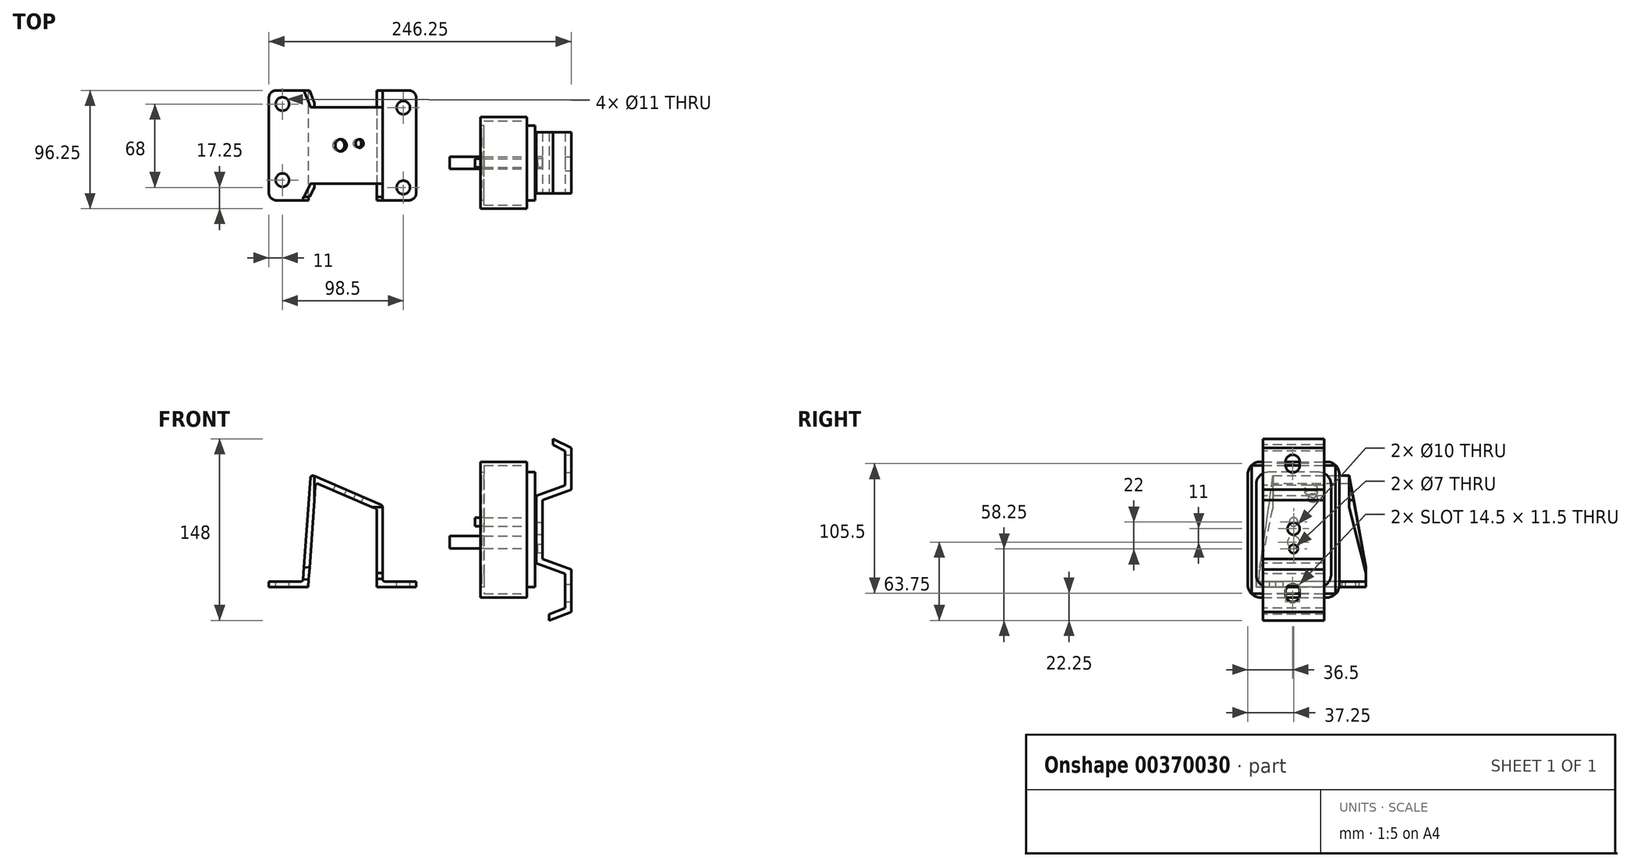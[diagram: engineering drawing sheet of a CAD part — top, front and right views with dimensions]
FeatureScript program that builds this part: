
annotation { "Feature Type Name" : "Feature", "Feature Type Description" : "" }
export const myFeature = defineFeature(function(context is Context, id is Id, definition is map)
    precondition{}
    {
        {
            var Q0;
            Q0=qCreatedBy(makeId("Front.planeOp"),FACE);
            var sketch = newSketch(context, id + "F0", { "sketchPlane" : qUnion([Q0])});
            skLineSegment(sketch, "E0", {"start": v(0, 0) * mm, "end": v(-120, 0) * mm});
            skPoint(sketch, "E1", {"position": v(-60, 0) * mm});
            skPoint(sketch, "E2", {"position": v(-32, 0) * mm});
            skPoint(sketch, "E3", {"position": v(-88, 0) * mm});
            skLineSegment(sketch, "E4", {"start": v(-32, 0) * mm, "end": v(-32, 63.5) * mm});
            skPoint(sketch, "E5", {"position": v(-82, 85) * mm});
            skLineSegment(sketch, "E6", {"start": v(-82, 85) * mm, "end": v(-88, 0) * mm});
            skLineSegment(sketch, "E7", {"start": v(-82, 85) * mm, "end": v(-32, 63.5) * mm});
            skLineSegment(sketch, "E8.0", {"start": v(-86.04, 91.64) * mm, "end": v(-92.49, 0.32) * mm});
            skLineSegment(sketch, "E8.1", {"start": v(-86.04, 91.64) * mm, "end": v(-27.5, 66.46) * mm});
            skLineSegment(sketch, "E8.2", {"start": v(-27.5, 0) * mm, "end": v(-27.5, 66.46) * mm});
            skLineSegment(sketch, "E9", {"start": v(-32, 0) * mm, "end": v(-27.5, 0) * mm});
            skPoint(sketch, "E10", {"position": v(-92.5, 0) * mm});
            skLineSegment(sketch, "E11", {"start": v(-92.5, 0) * mm, "end": v(-92.49, 0.32) * mm});
            skLineSegment(sketch, "E12", {"start": v(0, 0) * mm, "end": v(0, 4.5) * mm});
            skLineSegment(sketch, "E13", {"start": v(0, 4.5) * mm, "end": v(-27.5, 4.5) * mm});
            skLineSegment(sketch, "E14", {"start": v(-120, 0) * mm, "end": v(-120, 4.5) * mm});
            skLineSegment(sketch, "E15", {"start": v(-120, 4.5) * mm, "end": v(-92.2, 4.5) * mm});
            skSolve(sketch);
        }
        {
            var Q0;
            Q0=makeQuery(id+"F0.imprint","IMPRINT",FACE,{"disambiguationData":[TD([[makeQuery(id+"F0.imprint","IMPRINT",EDGE,{"derivedFrom":sQuery(id+"F0.wireOp",EDGE,"E4")}),-1.0]])]});
            var Q1;
            {var subQ0=sQuery(id+"F0.wireOp",EDGE,"E12");Q1=makeQuery(id+"F0.imprint","IMPRINT",FACE,{"disambiguationData":[TD([[makeQuery(id+"F0.imprint","IMPRINT",EDGE,{"derivedFrom":subQ0}),1.0]])]});}
            var Q2;
            {var subQ1=sQuery(id+"F0.wireOp",EDGE,"E11");Q2=makeQuery(id+"F0.imprint","IMPRINT",FACE,{"disambiguationData":[TD([[makeQuery(id+"F0.imprint","IMPRINT",EDGE,{"derivedFrom":subQ1}),1.0]])]});}
            extrude(context, id + "F1", {"entities" : qUnion([Q0, Q1, Q2]), "oppositeDirection" : true, "depth" : 89.5 * mm});
        }
        {
            var Q0;
            Q0=makeQuery(id+"F1.opExtrude","SWEPT_EDGE",EDGE,{"disambiguationData":[OSD([sQuery(id+"F0.wireOp",EDGE,"E8.0"),sQuery(id+"F0.wireOp",EDGE,"E8.1")])]});
            var Q1;
            Q1=makeQuery(id+"F1.opExtrude","SWEPT_EDGE",EDGE,{"disambiguationData":[OSD([sQuery(id+"F0.wireOp",EDGE,"E6"),sQuery(id+"F0.wireOp",EDGE,"E7")])]});
            var Q2;
            Q2=makeQuery(id+"F1.opExtrude","SWEPT_EDGE",EDGE,{"disambiguationData":[OSD([sQuery(id+"F0.wireOp",EDGE,"E4"),sQuery(id+"F0.wireOp",EDGE,"E7")])]});
            var Q3;
            Q3=makeQuery(id+"F1.opExtrude","SWEPT_EDGE",EDGE,{"disambiguationData":[OSD([sQuery(id+"F0.wireOp",EDGE,"E8.1"),sQuery(id+"F0.wireOp",EDGE,"E8.2")])]});
            var Q4;
            Q4=makeQuery(id+"F1.opExtrude","SWEPT_EDGE",EDGE,{"disambiguationData":[OSD([sQuery(id+"F0.wireOp",EDGE,"E8.0"),sQuery(id+"F0.wireOp",EDGE,"E15")])]});
            var Q5;
            Q5=makeQuery(id+"F1.opExtrude","SWEPT_EDGE",EDGE,{"disambiguationData":[OSD([sQuery(id+"F0.wireOp",EDGE,"E8.2"),sQuery(id+"F0.wireOp",EDGE,"E13")])]});
            fillet(context, id + "F2", {"entities" : qUnion([Q0, Q1, Q2, Q3, Q4, Q5]), "radius" : 2 * mm, "tangentPropagation" : true, "allowEdgeOverflow" : false});
        }
        {
            var Q0;
            Q0=makeQuery(id+"F1.opExtrude","SWEPT_FACE",FACE,{"disambiguationData":[OSD([sQuery(id+"F0.wireOp",EDGE,"E8.2")])]});
            var sketch = newSketch(context, id + "F3", { "sketchPlane" : qUnion([Q0])});
            skLineSegment(sketch, "E16.0", {"start": v(89.5, 90.52) * mm, "end": v(0, 90.52) * mm});
            skPoint(sketch, "E17", {"position": v(44.75, 90.52) * mm});
            skPoint(sketch, "E18", {"position": v(75.85, 90.52) * mm});
            skPoint(sketch, "E19", {"position": v(13.65, 90.52) * mm});
            skLineSegment(sketch, "E20.0", {"start": v(89.5, 65.15) * mm, "end": v(0, 65.15) * mm});
            skLineSegment(sketch, "E21.0", {"start": v(0, 6.5) * mm, "end": v(89.5, 6.5) * mm});
            skPoint(sketch, "E22", {"position": v(44.75, 6.5) * mm});
            skPoint(sketch, "E23", {"position": v(2.75, 6.5) * mm});
            skLineSegment(sketch, "E24", {"start": v(13.65, 90.52) * mm, "end": v(13.65, 65.15) * mm});
            skLineSegment(sketch, "E25", {"start": v(75.85, 90.52) * mm, "end": v(75.85, 65.15) * mm});
            skLineSegment(sketch, "E26.0", {"start": v(0, 6.5) * mm, "end": v(0, 65.15) * mm});
            skLineSegment(sketch, "E27.0", {"start": v(89.5, 6.5) * mm, "end": v(89.5, 65.15) * mm});
            skLineSegment(sketch, "E28.0", {"start": v(0, 90.52) * mm, "end": v(0, 66.98) * mm});
            skLineSegment(sketch, "E29.0", {"start": v(89.5, 90.52) * mm, "end": v(89.5, 66.98) * mm});
            skLineSegment(sketch, "E30", {"start": v(0, 66.98) * mm, "end": v(0, 65.15) * mm});
            skLineSegment(sketch, "E31", {"start": v(89.5, 66.98) * mm, "end": v(89.5, 65.15) * mm});
            skLineSegment(sketch, "E32", {"start": v(0, 90.52) * mm, "end": v(0, 93.52) * mm});
            skLineSegment(sketch, "E33", {"start": v(89.5, 6.5) * mm, "end": v(89.5, 11.5) * mm});
            skLineSegment(sketch, "E34", {"start": v(2.75, 6.5) * mm, "end": v(2.75, 11.5) * mm});
            skLineSegment(sketch, "E35", {"start": v(2.75, 11.5) * mm, "end": v(13.65, 65.15) * mm});
            skLineSegment(sketch, "E36", {"start": v(75.85, 65.15) * mm, "end": v(89.5, 11.5) * mm});
            skSolve(sketch);
        }
        {
            var Q0;
            {var subQ0=sQuery(id+"F3.wireOp",EDGE,"E25");Q0=makeQuery(id+"F3.imprint","IMPRINT",FACE,{"disambiguationData":[TD([[makeQuery(id+"F3.imprint","IMPRINT",EDGE,{"derivedFrom":subQ0}),1.0]])]});}
            var Q1;
            {var subQ0=sQuery(id+"F3.wireOp",EDGE,"E27.0");Q1=makeQuery(id+"F3.imprint","IMPRINT",FACE,{"disambiguationData":[TD([[makeQuery(id+"F3.imprint","IMPRINT",EDGE,{"derivedFrom":subQ0}),1.0]])]});}
            var Q2;
            {var subQ1=sQuery(id+"F3.wireOp",EDGE,"E26.0");Q2=makeQuery(id+"F3.imprint","IMPRINT",FACE,{"disambiguationData":[TD([[makeQuery(id+"F3.imprint","IMPRINT",EDGE,{"derivedFrom":subQ1}),-1.0]])]});}
            var Q3;
            {var subQ0=sQuery(id+"F3.wireOp",EDGE,"E24");Q3=makeQuery(id+"F3.imprint","IMPRINT",FACE,{"disambiguationData":[TD([[makeQuery(id+"F3.imprint","IMPRINT",EDGE,{"derivedFrom":subQ0}),-1.0]])]});}
            extrude(context, id + "F4", {"entities" : qUnion([Q0, Q1, Q2, Q3]), "operationType" : NewBodyOperationType.REMOVE, "oppositeDirection" : true, "depth" : 55.5 * mm});
        }
        {
            var Q0;
            Q0=makeQuery(id+"F4.boolean.opBoolean","COPY",EDGE,{"derivedFrom":makeQuery(id+"F4.opExtrude","SWEPT_EDGE",EDGE,{"disambiguationData":[OSD([sQuery(id+"F3.wireOp",EDGE,"E21.0"),sQuery(id+"F3.wireOp",EDGE,"E34")])]})});
            fillet(context, id + "F5", {"entities" : qUnion([Q0]), "radius" : 3 * mm, "tangentPropagation" : true, "allowEdgeOverflow" : false});
        }
        {
            var Q0;
            Q0=makeQuery(id+"F1.opExtrude","SWEPT_FACE",FACE,{"disambiguationData":[OSD([sQuery(id+"F0.wireOp",EDGE,"E8.0")])]});
            var sketch = newSketch(context, id + "F6", { "sketchPlane" : qUnion([Q0])});
            skLineSegment(sketch, "E37.0", {"start": v(-13.65, 84.26) * mm, "end": v(-13.65, 64.81) * mm});
            skLineSegment(sketch, "E38.0", {"start": v(-75.85, 84.26) * mm, "end": v(-75.85, 64.81) * mm});
            skLineSegment(sketch, "E39.1", {"start": v(-89.5, 4.55) * mm, "end": v(-89.5, 9.54) * mm});
            skLineSegment(sketch, "E40.0", {"start": v(-2.75, 7.53) * mm, "end": v(-2.75, 9.54) * mm});
            skLineSegment(sketch, "E41", {"start": v(-75.85, 84.26) * mm, "end": v(-89.5, 9.54) * mm});
            skLineSegment(sketch, "E42", {"start": v(-13.65, 84.26) * mm, "end": v(-2.75, 9.54) * mm});
            skLineSegment(sketch, "E43.0", {"start": v(-89.5, -0.14) * mm, "end": v(0, -0.14) * mm});
            skLineSegment(sketch, "E44", {"start": v(-2.75, 7.53) * mm, "end": v(-2.75, -0.14) * mm});
            skLineSegment(sketch, "E45.0", {"start": v(-89.5, 82.53) * mm, "end": v(-89.5, -0.14) * mm});
            skLineSegment(sketch, "E46.0", {"start": v(0, 82.53) * mm, "end": v(0, -0.14) * mm});
            skLineSegment(sketch, "E47.0", {"start": v(-89.5, 84.42) * mm, "end": v(0, 84.42) * mm});
            skLineSegment(sketch, "E48.0", {"start": v(-89.5, 82.53) * mm, "end": v(-89.5, 84.53) * mm});
            skLineSegment(sketch, "E49.0", {"start": v(0, 84.53) * mm, "end": v(0, 82.53) * mm});
            skLineSegment(sketch, "E50", {"start": v(-89.5, 84.42) * mm, "end": v(-89.5, 87.42) * mm});
            skLineSegment(sketch, "E51", {"start": v(-89.5, 87.42) * mm, "end": v(0, 87.42) * mm});
            skLineSegment(sketch, "E52", {"start": v(0, 87.42) * mm, "end": v(0, 84.42) * mm});
            skLineSegment(sketch, "E53", {"start": v(-13.65, 84.26) * mm, "end": v(-13.65, 87.42) * mm});
            skLineSegment(sketch, "E54", {"start": v(-75.85, 84.26) * mm, "end": v(-75.85, 87.42) * mm});
            skSolve(sketch);
        }
        {
            var Q0;
            {var subQ0=sQuery(id+"F6.wireOp",EDGE,"E45.0");var subQ1=sQuery(id+"F6.wireOp",EDGE,"E41");var subQ2=makeQuery(id+"F6.imprint","INTERSECT",VERTEX,{"derivedFrom":[subQ1,subQ0]});Q0=makeQuery(id+"F6.imprint","IMPRINT",FACE,{"disambiguationData":[TD([[makeQuery(id+"F6.imprint","IMPRINT",EDGE,{"disambiguationData":[TD([[subQ2,1.0]])],"derivedFrom":subQ1}),-1.0]])]});}
            var Q1;
            {var subQ0=sQuery(id+"F6.wireOp",EDGE,"E50");var subQ5=sQuery(id+"F6.wireOp",EDGE,"E51");var subQ6=makeQuery(id+"F6.imprint","INTERSECT",VERTEX,{"derivedFrom":[subQ0,subQ5]});Q1=makeQuery(id+"F6.imprint","IMPRINT",FACE,{"disambiguationData":[TD([[makeQuery(id+"F6.imprint","IMPRINT",EDGE,{"disambiguationData":[TD([[subQ6,-1.0]])],"derivedFrom":subQ5}),-1.0]])]});}
            var Q2;
            {var subQ8=sQuery(id+"F6.wireOp",EDGE,"E48.0");Q2=makeQuery(id+"F6.imprint","IMPRINT",FACE,{"disambiguationData":[TD([[makeQuery(id+"F6.imprint","IMPRINT",EDGE,{"derivedFrom":subQ8}),-1.0]])]});}
            var Q3;
            {var subQ0=sQuery(id+"F6.wireOp",EDGE,"E52");var subQ5=sQuery(id+"F6.wireOp",EDGE,"E51");var subQ6=makeQuery(id+"F6.imprint","INTERSECT",VERTEX,{"derivedFrom":[subQ5,subQ0]});Q3=makeQuery(id+"F6.imprint","IMPRINT",FACE,{"disambiguationData":[TD([[makeQuery(id+"F6.imprint","IMPRINT",EDGE,{"disambiguationData":[TD([[subQ6,1.0]])],"derivedFrom":subQ5}),-1.0]])]});}
            var Q4;
            {var subQ5=sQuery(id+"F6.wireOp",EDGE,"E49.0");Q4=makeQuery(id+"F6.imprint","IMPRINT",FACE,{"disambiguationData":[TD([[makeQuery(id+"F6.imprint","IMPRINT",EDGE,{"derivedFrom":subQ5}),-1.0]])]});}
            var Q5;
            {var subQ4=sQuery(id+"F6.wireOp",EDGE,"E40.0");Q5=makeQuery(id+"F6.imprint","IMPRINT",FACE,{"disambiguationData":[TD([[makeQuery(id+"F6.imprint","IMPRINT",EDGE,{"derivedFrom":subQ4}),-1.0]])]});}
            extrude(context, id + "F7", {"entities" : qUnion([Q0, Q1, Q2, Q3, Q4, Q5]), "operationType" : NewBodyOperationType.REMOVE, "oppositeDirection" : true, "depth" : 25 * mm});
        }
        {
            var Q0;
            Q0=makeQuery(id+"F1.opExtrude","SWEPT_FACE",FACE,{"disambiguationData":[OSD([sQuery(id+"F0.wireOp",EDGE,"E13")])]});
            var sketch = newSketch(context, id + "F8", { "sketchPlane" : qUnion([Q0])});
            skPoint(sketch, "E55", {"position": v(-10.5, 75.5) * mm});
            skPoint(sketch, "E56", {"position": v(-10.5, 10.5) * mm});
            skCircle(sketch, "E57", {"center": v(-10.5, 10.5) * mm, "radius": 5.5 * mm});
            skCircle(sketch, "E58", {"center": v(-10.5, 75.5) * mm, "radius": 5.5 * mm});
            skSolve(sketch);
        }
        {
            var Q0;
            Q0=qSketchRegion(id+"F8",true);
            extrude(context, id + "F9", {"entities" : qUnion([Q0]), "operationType" : NewBodyOperationType.REMOVE, "oppositeDirection" : true, "depth" : 5 * mm});
        }
        {
            var Q0;
            Q0=makeQuery(id+"F1.opExtrude","SWEPT_FACE",FACE,{"disambiguationData":[OSD([sQuery(id+"F0.wireOp",EDGE,"E15")])]});
            var sketch = newSketch(context, id + "F10", { "sketchPlane" : qUnion([Q0])});
            skPoint(sketch, "E59", {"position": v(-109, 78.5) * mm});
            skPoint(sketch, "E60", {"position": v(-109, 16.5) * mm});
            skCircle(sketch, "E61", {"center": v(-109, 16.5) * mm, "radius": 5.5 * mm});
            skCircle(sketch, "E62", {"center": v(-109, 78.5) * mm, "radius": 5.5 * mm});
            skSolve(sketch);
        }
        {
            var Q0;
            Q0=qSketchRegion(id+"F10",true);
            extrude(context, id + "F11", {"entities" : qUnion([Q0]), "operationType" : NewBodyOperationType.REMOVE, "oppositeDirection" : true, "depth" : 5 * mm});
        }
        {
            var Q0;
            Q0=makeQuery(id+"F1.opExtrude","SWEPT_FACE",FACE,{"disambiguationData":[OSD([sQuery(id+"F0.wireOp",EDGE,"E8.1")])]});
            var sketch = newSketch(context, id + "F12", { "sketchPlane" : qUnion([Q0])});
            skPoint(sketch, "E63", {"position": v(-88.32, 44.85) * mm});
            skCircle(sketch, "E64", {"center": v(-88.32, 44.85) * mm, "radius": 5 * mm});
            skPoint(sketch, "E65", {"position": v(-71.82, 46.35) * mm});
            skCircle(sketch, "E66", {"center": v(-71.82, 46.35) * mm, "radius": 3.5 * mm});
            skSolve(sketch);
        }
        {
            var Q0;
            Q0=qSketchRegion(id+"F12",true);
            extrude(context, id + "F13", {"entities" : qUnion([Q0]), "operationType" : NewBodyOperationType.REMOVE, "oppositeDirection" : true, "depth" : 5 * mm});
        }
        {
            var Q0;
            Q0=makeQuery(id+"F1.opExtrude","CAP_EDGE",EDGE,{"disambiguationData":[OSD([sQuery(id+"F0.wireOp",EDGE,"E12")])],"isStart":false});
            var Q1;
            Q1=makeQuery(id+"F1.opExtrude","CAP_EDGE",EDGE,{"disambiguationData":[OSD([sQuery(id+"F0.wireOp",EDGE,"E12")])],"isStart":true});
            var Q2;
            Q2=makeQuery(id+"F1.opExtrude","CAP_EDGE",EDGE,{"disambiguationData":[OSD([sQuery(id+"F0.wireOp",EDGE,"E14")])],"isStart":true});
            var Q3;
            Q3=makeQuery(id+"F1.opExtrude","CAP_EDGE",EDGE,{"disambiguationData":[OSD([sQuery(id+"F0.wireOp",EDGE,"E14")])],"isStart":false});
            fillet(context, id + "F14", {"entities" : qUnion([Q0, Q1, Q2, Q3]), "radius" : 6 * mm, "tangentPropagation" : true, "allowEdgeOverflow" : false});
        }
        {
            var Q0;
            Q0=qCreatedBy(makeId("Front.planeOp"),FACE);
            var sketch = newSketch(context, id + "F15", { "sketchPlane" : qUnion([Q0])});
            skPoint(sketch, "E67", {"position": v(75, 0) * mm});
            skLineSegment(sketch, "E68", {"start": v(75, 0) * mm, "end": v(96.75, 0) * mm});
            skLineSegment(sketch, "E69", {"start": v(75, 0) * mm, "end": v(53.25, 0) * mm});
            skLineSegment(sketch, "E70", {"start": v(53.25, 0) * mm, "end": v(53.25, 93.5) * mm});
            skLineSegment(sketch, "E71", {"start": v(53.25, 93.5) * mm, "end": v(96.75, 93.5) * mm});
            skLineSegment(sketch, "E72", {"start": v(96.75, 93.5) * mm, "end": v(96.75, 0) * mm});
            skSolve(sketch);
        }
        {
            var Q0;
            Q0=qSketchRegion(id+"F15",true);
            extrude(context, id + "F16", {"entities" : qUnion([Q0]), "oppositeDirection" : true, "depth" : 61 * mm});
        }
        {
            var Q0;
            Q0=makeQuery(id+"F16.opExtrude","SWEPT_FACE",FACE,{"disambiguationData":[OSD([sQuery(id+"F15.wireOp",EDGE,"E72")])]});
            var sketch = newSketch(context, id + "F17", { "sketchPlane" : qUnion([Q0])});
            skPoint(sketch, "E73", {"position": v(30.5, 47.5) * mm});
            skCircle(sketch, "E74", {"center": v(30.5, 47.5) * mm, "radius": 5 * mm});
            skPoint(sketch, "E75", {"position": v(30.5, 31) * mm});
            skCircle(sketch, "E76", {"center": v(30.5, 31) * mm, "radius": 3.5 * mm});
            skSolve(sketch);
        }
        {
            var Q0;
            Q0=makeQuery(id+"F17.imprint","IMPRINT",FACE,{"disambiguationData":[TD([[makeQuery(id+"F17.imprint","IMPRINT",EDGE,{"derivedFrom":sQuery(id+"F17.wireOp",EDGE,"E74")}),1.0]])]});
            extrude(context, id + "F18", {"entities" : qUnion([Q0]), "operationType" : NewBodyOperationType.ADD, "depth" : 20 * mm});
        }
        {
            var Q0;
            Q0=qSketchRegion(id+"F17",true);
            extrude(context, id + "F19", {"entities" : qUnion([Q0]), "operationType" : NewBodyOperationType.ADD, "depth" : 2.25 * mm});
        }
        {
            var Q0;
            Q0=makeQuery(id+"F16.opExtrude","SWEPT_FACE",FACE,{"disambiguationData":[OSD([sQuery(id+"F15.wireOp",EDGE,"E70")])]});
            var sketch = newSketch(context, id + "F20", { "sketchPlane" : qUnion([Q0])});
            skPoint(sketch, "E77", {"position": v(-30.5, 36.5) * mm});
            skPoint(sketch, "E78", {"position": v(-30.5, 53) * mm});
            skCircle(sketch, "E79", {"center": v(-30.5, 36.5) * mm, "radius": 5 * mm});
            skCircle(sketch, "E80", {"center": v(-30.5, 53) * mm, "radius": 3.5 * mm});
            skSolve(sketch);
        }
        {
            var Q0;
            Q0=makeQuery(id+"F20.imprint","IMPRINT",FACE,{"disambiguationData":[TD([[makeQuery(id+"F20.imprint","IMPRINT",EDGE,{"derivedFrom":sQuery(id+"F20.wireOp",EDGE,"E79")}),1.0]])]});
            extrude(context, id + "F21", {"entities" : qUnion([Q0]), "operationType" : NewBodyOperationType.ADD, "depth" : 26 * mm});
        }
        {
            var Q0;
            Q0=qSketchRegion(id+"F20",true);
            extrude(context, id + "F22", {"entities" : qUnion([Q0]), "operationType" : NewBodyOperationType.ADD, "depth" : 5.5 * mm});
        }
        {
            var Q0;
            Q0=makeQuery(id+"F16.opExtrude","CAP_EDGE",EDGE,{"disambiguationData":[OSD([sQuery(id+"F15.wireOp",EDGE,"E71")])],"isStart":true});
            var Q1;
            Q1=makeQuery(id+"F16.opExtrude","CAP_EDGE",EDGE,{"disambiguationData":[OSD([sQuery(id+"F15.wireOp",EDGE,"E71")])],"isStart":false});
            var Q2;
            Q2=makeQuery(id+"F16.opExtrude","CAP_EDGE",EDGE,{"disambiguationData":[OSD([sQuery(id+"F15.wireOp",EDGE,"E68"),sQuery(id+"F15.wireOp",EDGE,"E69")])],"isStart":false});
            var Q3;
            Q3=makeQuery(id+"F16.opExtrude","CAP_EDGE",EDGE,{"disambiguationData":[OSD([sQuery(id+"F15.wireOp",EDGE,"E68"),sQuery(id+"F15.wireOp",EDGE,"E69")])],"isStart":true});
            fillet(context, id + "F23", {"entities" : qUnion([Q0, Q1, Q2, Q3]), "radius" : 10 * mm, "tangentPropagation" : true, "allowEdgeOverflow" : false});
        }
        {
            var Q0;
            Q0=makeQuery(id+"F16.opExtrude","SWEPT_FACE",FACE,{"disambiguationData":[OSD([sQuery(id+"F15.wireOp",EDGE,"E70")])]});
            cPlane(context, id + "F24", {"entities" : qUnion([Q0]), "cplaneType" : CPlaneType.OFFSET, "offset" : 1 * mm, "width" : 150 * mm, "height" : 150 * mm});
        }
        {
            var Q0;
            Q0=qCreatedBy(id+"F24.planeOp",FACE);
            var sketch = newSketch(context, id + "F25", { "sketchPlane" : qUnion([Q0])});
            skLineSegment(sketch, "E81.0", {"start": v(-51, 93.5) * mm, "end": v(-10, 93.5) * mm});
            skLineSegment(sketch, "E82.0", {"start": v(-61, 10) * mm, "end": v(-61, 83.5) * mm});
            skPoint(sketch, "E83", {"position": v(-30.5, 46.75) * mm});
            skPoint(sketch, "E83.positionSnap0", {"position": v(-61, 46.75) * mm});
            skPoint(sketch, "E83.positionSnap1", {"position": v(-30.5, 93.5) * mm});
            skLineSegment(sketch, "E84.bottom", {"start": v(6.75, 102) * mm, "end": v(-67.75, 102) * mm});
            skLineSegment(sketch, "E84.top", {"start": v(6.75, -8.5) * mm, "end": v(-67.75, -8.5) * mm});
            skLineSegment(sketch, "E84.left", {"start": v(6.75, 102) * mm, "end": v(6.75, -8.5) * mm});
            skLineSegment(sketch, "E84.right", {"start": v(-67.75, 102) * mm, "end": v(-67.75, -8.5) * mm});
            skCircle(sketch, "E85.0", {"center": v(-30.5, 36.5) * mm, "radius": 5 * mm});
            skCircle(sketch, "E86.0", {"center": v(-30.5, 53) * mm, "radius": 3.5 * mm});
            skSolve(sketch);
        }
        {
            var Q0;
            Q0=qSketchRegion(id+"F25",true);
            extrude(context, id + "F26", {"entities" : qUnion([Q0]), "oppositeDirection" : true, "depth" : 38 * mm});
        }
        {
            var Q0;
            Q0=makeQuery(id+"F26.opExtrude","CAP_FACE",FACE,{"disambiguationData":[OSD([sQuery(id+"F25.wireOp",EDGE,"E84.bottom"),sQuery(id+"F25.wireOp",EDGE,"E84.top"),sQuery(id+"F25.wireOp",EDGE,"E84.left"),sQuery(id+"F25.wireOp",EDGE,"E84.right")])],"isStart":false});
            var sketch = newSketch(context, id + "F27", { "sketchPlane" : qUnion([Q0])});
            skLineSegment(sketch, "E87.0", {"start": v(-6.75, 102) * mm, "end": v(67.75, 102) * mm});
            skLineSegment(sketch, "E88.0", {"start": v(-6.75, 102) * mm, "end": v(-6.75, -8.5) * mm});
            skLineSegment(sketch, "E89.0", {"start": v(67.75, 102) * mm, "end": v(67.75, -8.5) * mm});
            skLineSegment(sketch, "E90.0", {"start": v(-6.75, -8.5) * mm, "end": v(67.75, -8.5) * mm});
            skLineSegment(sketch, "E91.0", {"start": v(-3.75, 99) * mm, "end": v(64.75, 99) * mm});
            skLineSegment(sketch, "E91.1", {"start": v(-3.75, 99) * mm, "end": v(-3.75, -5.5) * mm});
            skLineSegment(sketch, "E91.2", {"start": v(-3.75, -5.5) * mm, "end": v(64.75, -5.5) * mm});
            skLineSegment(sketch, "E91.3", {"start": v(64.75, 99) * mm, "end": v(64.75, -5.5) * mm});
            skSolve(sketch);
        }
        {
            var Q0;
            Q0=makeQuery(id+"F27.imprint","IMPRINT",FACE,{"disambiguationData":[TD([[makeQuery(id+"F27.imprint","IMPRINT",EDGE,{"derivedFrom":sQuery(id+"F27.wireOp",EDGE,"E91.0")}),-1.0]])]});
            extrude(context, id + "F28", {"entities" : qUnion([Q0]), "operationType" : NewBodyOperationType.REMOVE, "oppositeDirection" : true, "depth" : 35 * mm});
        }
        {
            var Q0;
            Q0=makeQuery(id+"F26.opExtrude","SWEPT_EDGE",EDGE,{"disambiguationData":[OSD([sQuery(id+"F25.wireOp",EDGE,"E84.bottom"),sQuery(id+"F25.wireOp",EDGE,"E84.left")])]});
            var Q1;
            Q1=makeQuery(id+"F26.opExtrude","SWEPT_EDGE",EDGE,{"disambiguationData":[OSD([sQuery(id+"F25.wireOp",EDGE,"E84.bottom"),sQuery(id+"F25.wireOp",EDGE,"E84.right")])]});
            var Q2;
            Q2=makeQuery(id+"F26.opExtrude","SWEPT_EDGE",EDGE,{"disambiguationData":[OSD([sQuery(id+"F25.wireOp",EDGE,"E84.top"),sQuery(id+"F25.wireOp",EDGE,"E84.right")])]});
            var Q3;
            Q3=makeQuery(id+"F26.opExtrude","SWEPT_EDGE",EDGE,{"disambiguationData":[OSD([sQuery(id+"F25.wireOp",EDGE,"E84.top"),sQuery(id+"F25.wireOp",EDGE,"E84.left")])]});
            fillet(context, id + "F29", {"entities" : qUnion([Q0, Q1, Q2, Q3]), "radius" : 10 * mm, "tangentPropagation" : true, "allowEdgeOverflow" : false});
        }
        {
            var Q0;
            Q0=makeQuery(id+"F16.opExtrude","SWEPT_FACE",FACE,{"disambiguationData":[OSD([sQuery(id+"F15.wireOp",EDGE,"E72")])]});
            cPlane(context, id + "F30", {"entities" : qUnion([Q0]), "cplaneType" : CPlaneType.OFFSET, "offset" : 1 * mm, "width" : 150 * mm, "height" : 150 * mm});
        }
        {
            var Q0;
            Q0=qCreatedBy(id+"F30.planeOp",FACE);
            var sketch = newSketch(context, id + "F31", { "sketchPlane" : qUnion([Q0])});
            skLineSegment(sketch, "E92.0", {"start": v(61, 83.5) * mm, "end": v(61, 10) * mm});
            skLineSegment(sketch, "E93.0", {"start": v(51, 0) * mm, "end": v(10, 0) * mm});
            skPoint(sketch, "E94", {"position": v(30.5, 46.75) * mm});
            skPoint(sketch, "E94.positionSnap0", {"position": v(30.5, 0) * mm});
            skPoint(sketch, "E94.positionSnap1", {"position": v(61, 46.75) * mm});
            skLineSegment(sketch, "E95.bottom", {"start": v(55.5, -27.25) * mm, "end": v(5.5, -27.25) * mm});
            skLineSegment(sketch, "E95.top", {"start": v(55.5, 120.75) * mm, "end": v(5.5, 120.75) * mm});
            skLineSegment(sketch, "E95.left", {"start": v(55.5, -27.25) * mm, "end": v(55.5, 120.75) * mm});
            skLineSegment(sketch, "E95.right", {"start": v(5.5, -27.25) * mm, "end": v(5.5, 120.75) * mm});
            skCircle(sketch, "E96.0.0", {"center": v(30.5, 31) * mm, "radius": 3.5 * mm});
            skCircle(sketch, "E97.0", {"center": v(30.5, 47.5) * mm, "radius": 5 * mm});
            skSolve(sketch);
        }
        {
            var Q0;
            Q0=qSketchRegion(id+"F31",true);
            extrude(context, id + "F32", {"entities" : qUnion([Q0]), "depth" : 28.5 * mm});
        }
        {
            var Q0;
            Q0=makeQuery(id+"F32.opExtrude","SWEPT_FACE",FACE,{"disambiguationData":[OSD([sQuery(id+"F31.wireOp",EDGE,"E95.right")])]});
            var sketch = newSketch(context, id + "F33", { "sketchPlane" : qUnion([Q0])});
            skLineSegment(sketch, "E98.0", {"start": v(126.25, -27.25) * mm, "end": v(126.25, 120.75) * mm});
            skPoint(sketch, "E99", {"position": v(97.75, 46.75) * mm});
            skPoint(sketch, "E100", {"position": v(97.75, 74.25) * mm});
            skPoint(sketch, "E101", {"position": v(97.75, 19.25) * mm});
            skPoint(sketch, "E102", {"position": v(121.25, -27.25) * mm});
            skLineSegment(sketch, "E103", {"start": v(121.25, -27.25) * mm, "end": v(121.25, 120.75) * mm, "construction": true});
            skPoint(sketch, "E104", {"position": v(121.25, 46.75) * mm});
            skPoint(sketch, "E105", {"position": v(121.25, 82.75) * mm});
            skPoint(sketch, "E106", {"position": v(121.25, 10.75) * mm});
            skPoint(sketch, "E107", {"position": v(121.25, -17.25) * mm});
            skPoint(sketch, "E108", {"position": v(121.25, 110.75) * mm});
            skLineSegment(sketch, "E109", {"start": v(97.75, 19.25) * mm, "end": v(121.25, 10.75) * mm});
            skLineSegment(sketch, "E110", {"start": v(121.25, 10.75) * mm, "end": v(121.25, -17.25) * mm});
            skLineSegment(sketch, "E111", {"start": v(97.75, 19.25) * mm, "end": v(97.75, 74.25) * mm});
            skLineSegment(sketch, "E112", {"start": v(97.75, 74.25) * mm, "end": v(121.25, 82.75) * mm});
            skLineSegment(sketch, "E113", {"start": v(121.25, 82.75) * mm, "end": v(121.25, 110.75) * mm});
            skPoint(sketch, "E114", {"position": v(111.25, 120.75) * mm});
            skPoint(sketch, "E115", {"position": v(108.25, -27.25) * mm});
            skLineSegment(sketch, "E116", {"start": v(108.25, -27.25) * mm, "end": v(108.25, -22.25) * mm});
            skLineSegment(sketch, "E117", {"start": v(108.25, -22.25) * mm, "end": v(121.25, -17.25) * mm});
            skLineSegment(sketch, "E118", {"start": v(111.25, 120.75) * mm, "end": v(111.25, 115.75) * mm});
            skLineSegment(sketch, "E119", {"start": v(111.25, 115.75) * mm, "end": v(121.25, 110.75) * mm});
            skLineSegment(sketch, "E120.1", {"start": v(102.75, 22.76) * mm, "end": v(102.75, 70.74) * mm});
            skLineSegment(sketch, "E121", {"start": v(108.25, -27.25) * mm, "end": v(126.25, -20.33) * mm});
            skLineSegment(sketch, "E122", {"start": v(111.25, 120.75) * mm, "end": v(126.25, 113.25) * mm});
            skLineSegment(sketch, "E123", {"start": v(126.25, 113.25) * mm, "end": v(126.25, -20.33) * mm});
            skLineSegment(sketch, "E124", {"start": v(102.75, 22.76) * mm, "end": v(126.25, 14.26) * mm});
            skLineSegment(sketch, "E125", {"start": v(102.75, 70.74) * mm, "end": v(126.25, 79.24) * mm});
            skLineSegment(sketch, "E126.0", {"start": v(126.25, 120.75) * mm, "end": v(97.75, 120.75) * mm});
            skLineSegment(sketch, "E127.0", {"start": v(97.75, -27.25) * mm, "end": v(97.75, 120.75) * mm});
            skLineSegment(sketch, "E128.0", {"start": v(126.25, -27.25) * mm, "end": v(97.75, -27.25) * mm});
            skSolve(sketch);
        }
        {
            var Q0;
            {var subQ3=sQuery(id+"F33.wireOp",EDGE,"E122");Q0=makeQuery(id+"F33.imprint","IMPRINT",FACE,{"disambiguationData":[TD([[makeQuery(id+"F33.imprint","IMPRINT",EDGE,{"derivedFrom":subQ3}),1.0]])]});}
            var Q1;
            {var subQ4=sQuery(id+"F33.wireOp",EDGE,"E112");Q1=makeQuery(id+"F33.imprint","IMPRINT",FACE,{"disambiguationData":[TD([[makeQuery(id+"F33.imprint","IMPRINT",EDGE,{"derivedFrom":subQ4}),1.0]])]});}
            var Q2;
            Q2=makeQuery(id+"F33.imprint","IMPRINT",FACE,{"disambiguationData":[TD([[makeQuery(id+"F33.imprint","IMPRINT",EDGE,{"derivedFrom":sQuery(id+"F33.wireOp",EDGE,"E120.1")}),-1.0]])]});
            var Q3;
            {var subQ1=sQuery(id+"F33.wireOp",EDGE,"E109");Q3=makeQuery(id+"F33.imprint","IMPRINT",FACE,{"disambiguationData":[TD([[makeQuery(id+"F33.imprint","IMPRINT",EDGE,{"derivedFrom":subQ1}),-1.0]])]});}
            var Q4;
            {var subQ3=sQuery(id+"F33.wireOp",EDGE,"E121");Q4=makeQuery(id+"F33.imprint","IMPRINT",FACE,{"disambiguationData":[TD([[makeQuery(id+"F33.imprint","IMPRINT",EDGE,{"derivedFrom":subQ3}),-1.0]])]});}
            extrude(context, id + "F34", {"entities" : qUnion([Q0, Q1, Q2, Q3, Q4]), "operationType" : NewBodyOperationType.REMOVE, "oppositeDirection" : true, "depth" : 50 * mm});
        }
        {
            var Q0;
            {var subQ0=sQuery(id+"F31.wireOp",EDGE,"E95.left");var subQ1=sQuery(id+"F31.wireOp",EDGE,"E95.right");Q0=makeQuery(id+"F34.boolean.opBoolean","SPLIT",FACE,{"disambiguationData":[TD([makeQuery(id+"F34.opExtrude","SWEPT_FACE",FACE,{"disambiguationData":[OSD([sQuery(id+"F33.wireOp",EDGE,"E122")])]})])],"derivedFrom":makeQuery(id+"F32.opExtrude","CAP_FACE",FACE,{"disambiguationData":[OSD([sQuery(id+"F31.wireOp",EDGE,"E95.bottom"),sQuery(id+"F31.wireOp",EDGE,"E95.top"),subQ0,subQ1,sQuery(id+"F31.wireOp",EDGE,"E96.0.0"),sQuery(id+"F31.wireOp",EDGE,"E97.0")])],"isStart":false})});}
            var sketch = newSketch(context, id + "F35", { "sketchPlane" : qUnion([Q0])});
            skPoint(sketch, "E129", {"position": v(35.5, -12.25) * mm});
            skLineSegment(sketch, "E130.bottom", {"start": v(29.75, -12.25) * mm, "end": v(29.75, -12.25) * mm});
            skLineSegment(sketch, "E130.top", {"start": v(29.75, 2.25) * mm, "end": v(29.75, 2.25) * mm});
            skLineSegment(sketch, "E130.left", {"start": v(35.5, -6.5) * mm, "end": v(35.5, -3.5) * mm});
            skLineSegment(sketch, "E130.right", {"start": v(24, -6.5) * mm, "end": v(24, -3.5) * mm});
            skPoint(sketch, "E131.visualSharp", {"position": v(24, -12.25) * mm});
            skArc(sketch, "E131.filletArc", {"start": v(24, -6.5) * mm, "mid": v(25.68, -10.57) * mm, "end": v(29.75, -12.25) * mm});
            skArc(sketch, "E132.filletArc", {"start": v(29.75, -12.25) * mm, "mid": v(33.82, -10.57) * mm, "end": v(35.5, -6.5) * mm});
            skPoint(sketch, "E133.visualSharp", {"position": v(24, 2.25) * mm});
            skArc(sketch, "E133.filletArc", {"start": v(29.75, 2.25) * mm, "mid": v(25.68, 0.57) * mm, "end": v(24, -3.5) * mm});
            skPoint(sketch, "E134.visualSharp", {"position": v(35.5, 2.25) * mm});
            skArc(sketch, "E134.filletArc", {"start": v(35.5, -3.5) * mm, "mid": v(33.82, 0.57) * mm, "end": v(29.75, 2.25) * mm});
            skPoint(sketch, "E135.endSnap0", {"position": v(5.5, 46.75) * mm});
            skLineSegment(sketch, "E136", {"start": v(29.75, 2.25) * mm, "end": v(29.75, 93.25) * mm});
            skLineSegment(sketch, "E137", {"start": v(29.75, 47.75) * mm, "end": v(39.75, 47.75) * mm});
            skPoint(sketch, "E137.endSnap0", {"position": v(29.75, 47.75) * mm});
            skArc(sketch, "E138.MirrorCS", {"start": v(29.75, 93.25) * mm, "mid": v(25.68, 94.93) * mm, "end": v(24, 99) * mm});
            skArc(sketch, "E139.MirrorCS", {"start": v(35.5, 99) * mm, "mid": v(33.82, 94.93) * mm, "end": v(29.75, 93.25) * mm});
            skLineSegment(sketch, "E140.MirrorCS", {"start": v(35.5, 102) * mm, "end": v(35.5, 99) * mm});
            skArc(sketch, "E141.MirrorCS", {"start": v(29.75, 107.75) * mm, "mid": v(33.82, 106.07) * mm, "end": v(35.5, 102) * mm});
            skArc(sketch, "E142.MirrorCS", {"start": v(24, 102) * mm, "mid": v(25.68, 106.07) * mm, "end": v(29.75, 107.75) * mm});
            skLineSegment(sketch, "E143.MirrorCS", {"start": v(24, 102) * mm, "end": v(24, 99) * mm});
            skSolve(sketch);
        }
        {
            var Q0;
            Q0=qSketchRegion(id+"F35",true);
            extrude(context, id + "F36", {"entities" : qUnion([Q0]), "operationType" : NewBodyOperationType.REMOVE, "oppositeDirection" : true, "depth" : 5 * mm});
        }
    });
